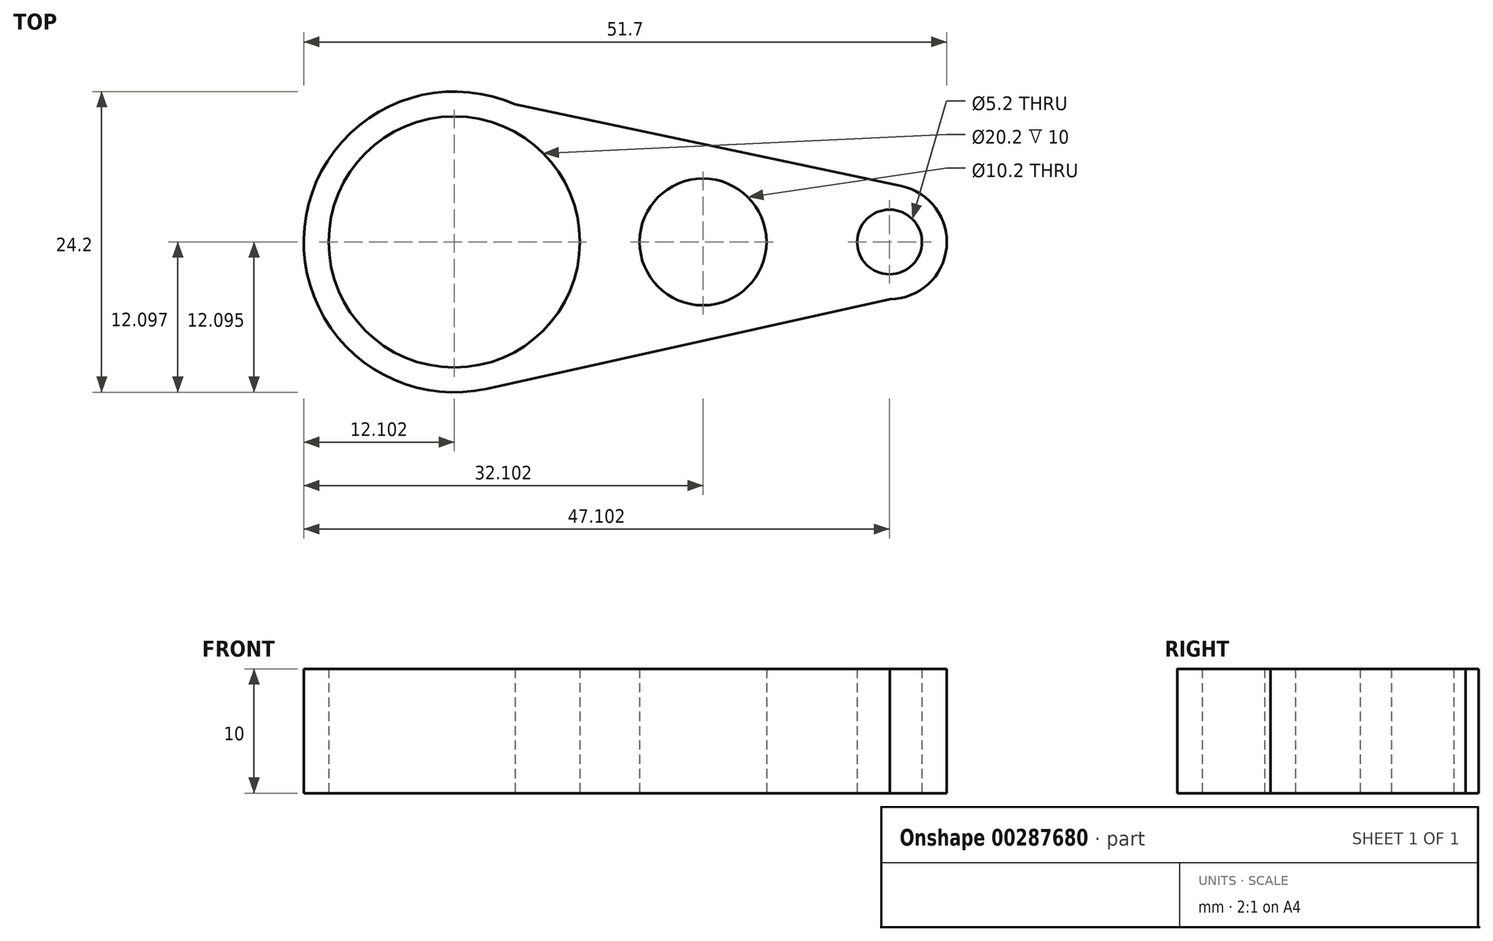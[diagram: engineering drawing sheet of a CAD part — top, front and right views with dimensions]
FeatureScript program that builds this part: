
annotation { "Feature Type Name" : "Feature", "Feature Type Description" : "" }
export const myFeature = defineFeature(function(context is Context, id is Id, definition is map)
    precondition{}
    {
        {
            var Q0;
            Q0=qCreatedBy(makeId("Top.planeOp"),FACE);
            var sketch = newSketch(context, id + "F0", { "sketchPlane" : qUnion([Q0])});
            skLineSegment(sketch, "E0", {"start": v(21, -4.56) * mm, "end": v(-11.4, -11.76) * mm});
            skLineSegment(sketch, "E1", {"start": v(-9.13, 11.11) * mm, "end": v(21.92, 4.55) * mm});
            skArc(sketch, "E2.0", {"start": v(-9.13, 11.11) * mm, "mid": v(-26.07, 1.24) * mm, "end": v(-11.4, -11.76) * mm});
            skArc(sketch, "E3.0", {"start": v(21, -4.56) * mm, "mid": v(25.55, -0.42) * mm, "end": v(21.92, 4.55) * mm});
            skCircle(sketch, "E4", {"center": v(20.97, 0.04) * mm, "radius": 2.6 * mm});
            skCircle(sketch, "E5", {"center": v(-14.03, 0.05) * mm, "radius": 10.1 * mm});
            skPoint(sketch, "E6.orphan", {"position": v(-14.03, -12.35) * mm});
            skCircle(sketch, "E7", {"center": v(5.97, 0.05) * mm, "radius": 5.1 * mm});
            skPoint(sketch, "E8.orphan", {"position": v(-14.03, 12.15) * mm});
            skSolve(sketch);
        }
        {
            var Q0;
            Q0=makeQuery(id+"F0.imprint","IMPRINT",FACE,{"disambiguationData":[TD([[makeQuery(id+"F0.imprint","IMPRINT",EDGE,{"derivedFrom":sQuery(id+"F0.wireOp",EDGE,"E0")}),-1.0]])]});
            extrude(context, id + "F1", {"entities" : qUnion([Q0]), "depth" : 10 * mm});
        }
    });
